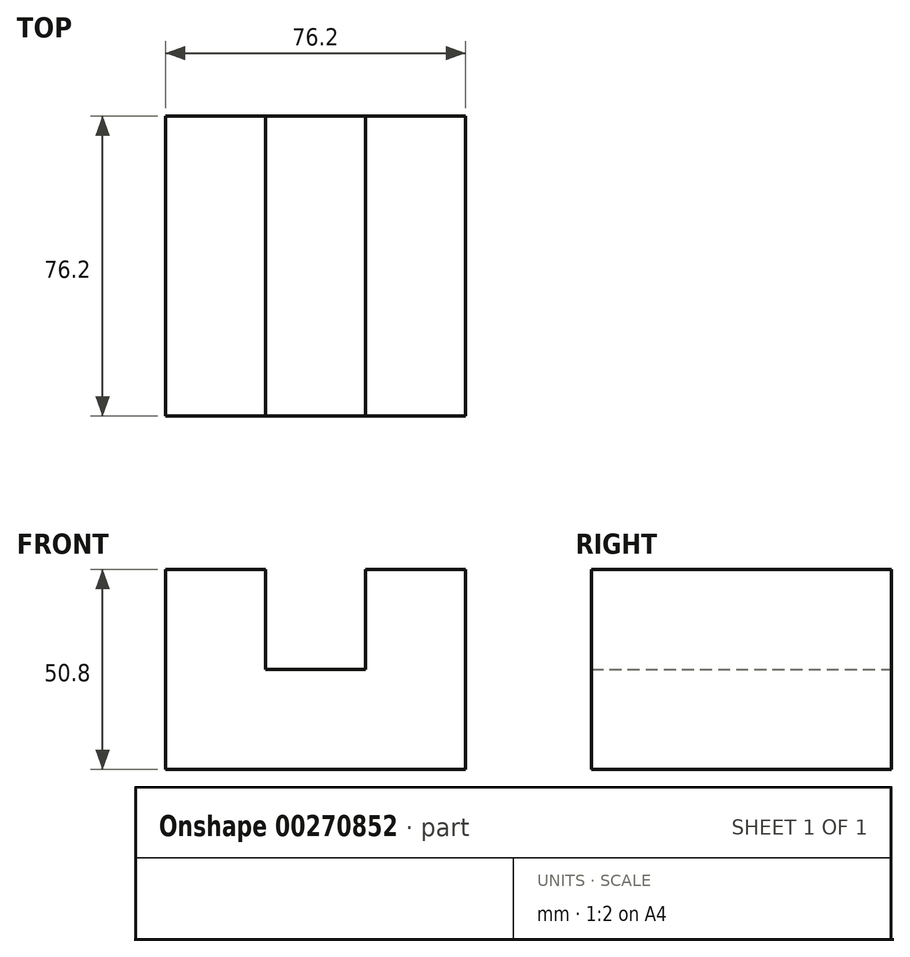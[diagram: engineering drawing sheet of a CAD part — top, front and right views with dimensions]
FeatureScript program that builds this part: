
annotation { "Feature Type Name" : "Feature", "Feature Type Description" : "" }
export const myFeature = defineFeature(function(context is Context, id is Id, definition is map)
    precondition{}
    {
        {
            var Q0;
            Q0=qCreatedBy(makeId("Front.planeOp"),FACE);
            var sketch = newSketch(context, id + "F0", { "sketchPlane" : qUnion([Q0])});
            skLineSegment(sketch, "E0", {"start": v(-71.61, 9.73) * mm, "end": v(4.59, 9.73) * mm});
            skLineSegment(sketch, "E1", {"start": v(4.59, 9.73) * mm, "end": v(4.59, 60.53) * mm});
            skLineSegment(sketch, "E2", {"start": v(-71.61, 9.73) * mm, "end": v(-71.61, 60.53) * mm});
            skLineSegment(sketch, "E3", {"start": v(-71.61, 60.53) * mm, "end": v(-46.21, 60.53) * mm});
            skLineSegment(sketch, "E4", {"start": v(4.59, 60.53) * mm, "end": v(-20.81, 60.53) * mm});
            skLineSegment(sketch, "E5", {"start": v(-20.81, 60.53) * mm, "end": v(-20.81, 35.13) * mm});
            skLineSegment(sketch, "E6", {"start": v(-46.21, 60.53) * mm, "end": v(-46.21, 35.13) * mm});
            skLineSegment(sketch, "E7", {"start": v(-46.21, 35.13) * mm, "end": v(-20.81, 35.13) * mm});
            skSolve(sketch);
        }
        {
            var Q0;
            Q0 = qSketchRegion(id + "F0", true);
            extrude(context, id + "F1", {"entities" : qUnion([Q0]), "depth" : 76.2 * mm});
        }
    });
